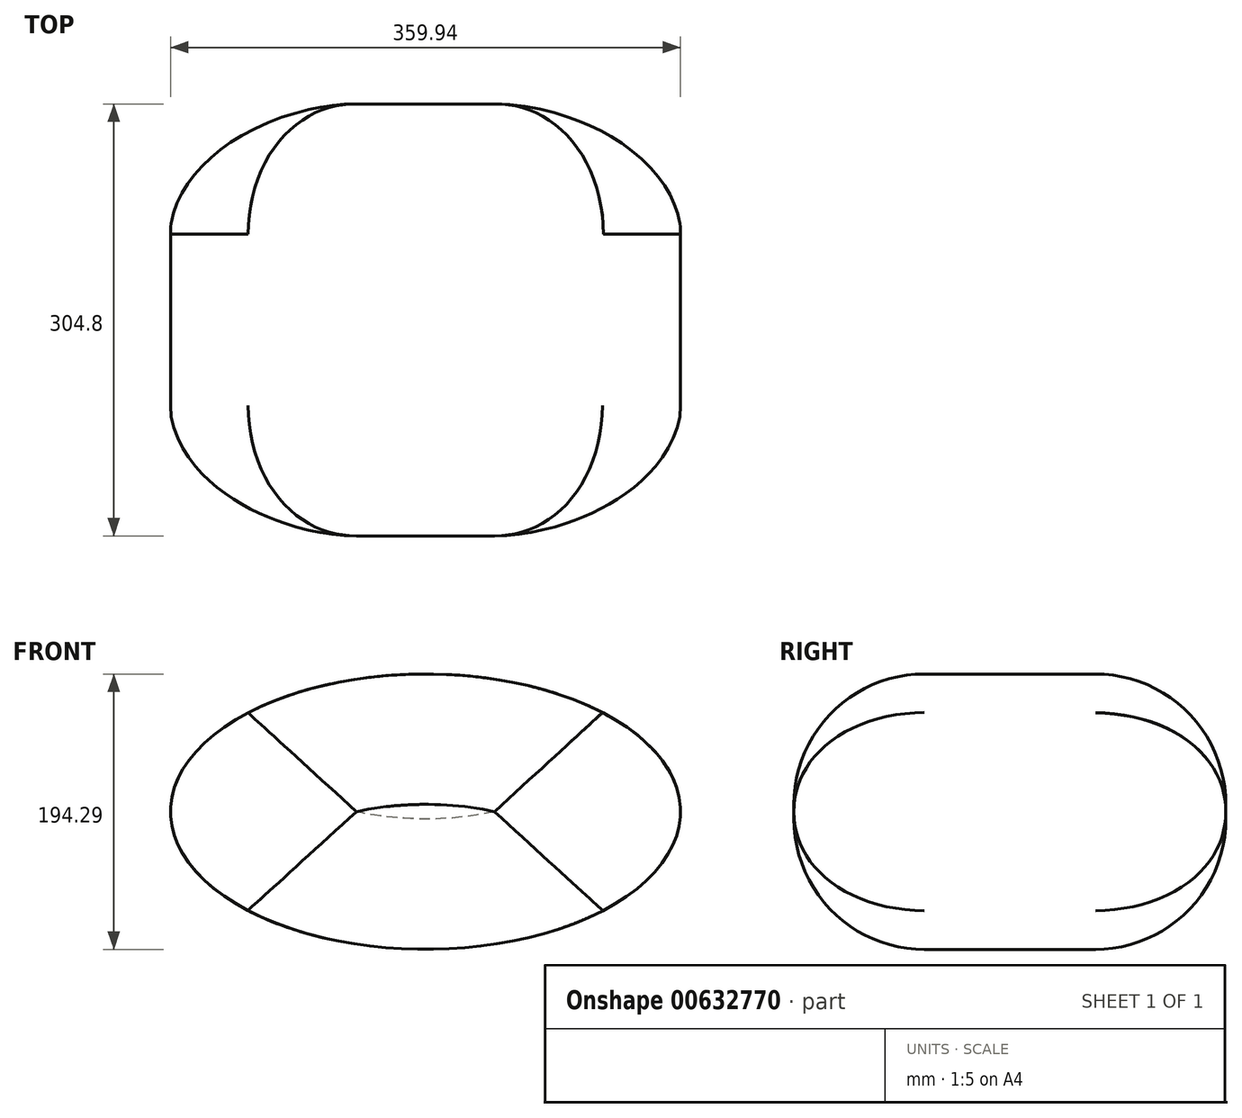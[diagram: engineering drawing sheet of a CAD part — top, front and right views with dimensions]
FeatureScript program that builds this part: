
annotation { "Feature Type Name" : "Feature", "Feature Type Description" : "" }
export const myFeature = defineFeature(function(context is Context, id is Id, definition is map)
    precondition{}
    {
        {
            var Q0;
            Q0=qCreatedBy(makeId("Front.planeOp"),FACE);
            var sketch = newSketch(context, id + "F0", { "sketchPlane" : qUnion([Q0])});
            skEllipse(sketch, "E0", {"center": v(-3.02, 7.63) * mm, "majorRadius": 179.97 * mm, "minorRadius": 97.14 * mm, "majorAxis": v(1, 0)});
            skSolve(sketch);
        }
        {
            var Q0;
            Q0 = qSketchRegion(id + "F0", true);
            extrude(context, id + "F1", {"entities" : qUnion([Q0]), "depth" : 304.8 * mm, "offsetDistance" : 25.4 * mm});
        }
        {
            var Q0;
            Q0=makeQuery(id+"F1.opExtrude","CAP_EDGE",EDGE,{"disambiguationData":[OSD([sQuery(id+"F0.wireOp",EDGE,"E0")])],"isStart":false});
            var Q1;
            Q1=makeQuery(id+"F1.opExtrude","CAP_EDGE",EDGE,{"disambiguationData":[OSD([sQuery(id+"F0.wireOp",EDGE,"E0")])],"isStart":true});
            fillet(context, id + "F2", {"entities" : qUnion([Q0, Q1]), "radius" : 91.98 * mm, "tangentPropagation" : true, "allowEdgeOverflow" : false});
        }
    });
